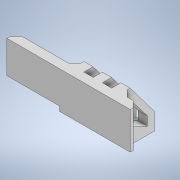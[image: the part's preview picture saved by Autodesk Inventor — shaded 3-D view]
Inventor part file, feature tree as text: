
AUTODESK INVENTOR PART (.ipt)
format: ipt  version: 2020.1 (Build 241239000, 239)  size: 218,112 bytes
history: native  units: mm
features: extrude x6, sketch x6, chamfer x2
ambient origin geometry x8: Origin, YZ Plane, XZ Plane, XY Plane, X Axis, Y Axis, Z Axis, Center Point
bodies: Solid1 (feature_tree)
feature tree (14):
  extrude  "Extrusion1"  Depth=14.0mm
  extrude  "Extrusion2"  Depth=5.0mm
  extrude  "Extrusion3"  Depth=10.0mm
  extrude  "Extrusion5"  Depth=1.0mm
  chamfer  "Chamfer1"  Distance=3.0mm
  chamfer  "Chamfer2"  Distance=12.0mm
  extrude  "Extrusion6"  Depth=2.0mm
  extrude  "Extrusion7"  Depth=2.0mm
  sketch  "Sketch1"  dims[d0=5.0mm d1=14.0mm]
  sketch  "Sketch2"  dims[d2=14.0mm d3=5.0mm]
  sketch  "Sketch3"  dims[d4=10.0mm d5=10.0mm]
  sketch  "Sketch4"  dims[d6=10.0mm d9=1.0mm]
  sketch  "Sketch5"  dims[d10=1.0mm]
  sketch  "Sketch6"  dims[d11=1.0mm d12=3.0mm d13=0.0mm d16=12.0mm d17=2.0mm d19=2.0mm d20=2.0mm d21=16.0mm d22=0.0mm d27=3.0mm d28=3.0mm d29=3.0mm d30=3.0mm d31=3.0mm d32=15.0mm d33=0.0mm d34=2.0mm d35=1.5mm d37=2.0mm d38=1.0mm d41=25.0mm d42=0.0mm d43=2.0mm d44=2.0mm d45=45.0deg d46=2.0mm d47=2.0mm d48=45.0deg d49=1.1mm d50=7.0mm d51=15.0mm d52=0.0mm d53=1.5mm d54=10.0mm d55=0.0mm d39=0.5mm d40=0.872665mm]
